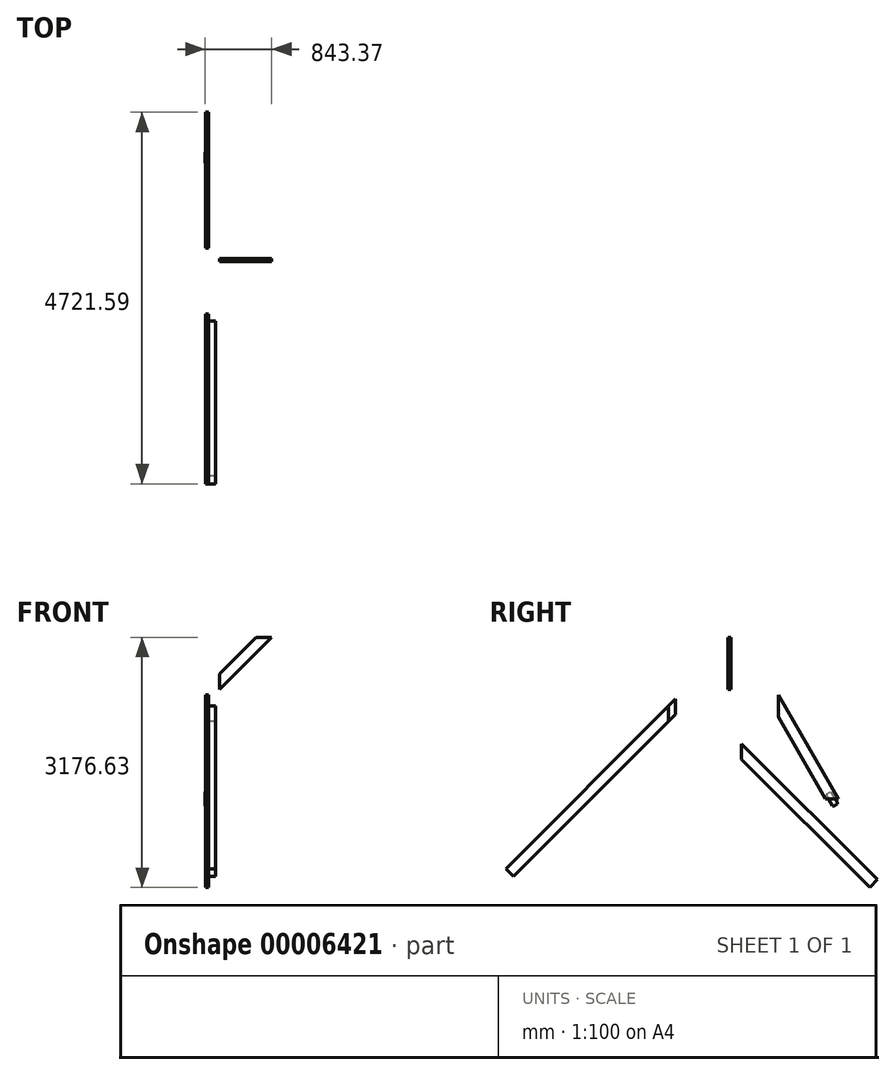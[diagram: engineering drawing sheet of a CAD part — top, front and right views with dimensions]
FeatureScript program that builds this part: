
annotation { "Feature Type Name" : "Feature", "Feature Type Description" : "" }
export const myFeature = defineFeature(function(context is Context, id is Id, definition is map)
    precondition{}
    {
        {
            var Q0;
            Q0=qCreatedBy(makeId("Front.planeOp"),FACE);
            var sketch = newSketch(context, id + "F0", { "sketchPlane" : qUnion([Q0])});
            skLineSegment(sketch, "E0", {"start": v(181.36, 197.57) * mm, "end": v(644.2, 660.4) * mm});
            skLineSegment(sketch, "E1", {"start": v(644.2, 660.4) * mm, "end": v(841.76, 660.4) * mm});
            skLineSegment(sketch, "E2", {"start": v(841.76, 660.4) * mm, "end": v(181.36, 0) * mm});
            skLineSegment(sketch, "E3", {"start": v(181.36, 0) * mm, "end": v(181.36, 197.57) * mm});
            skLineSegment(sketch, "E4", {"start": v(181.36, 0) * mm, "end": v(935.54, 0) * mm, "construction": true});
            skSolve(sketch);
        }
        {
            var Q0;
            Q0=makeQuery(id+"F0.imprint","IMPRINT",FACE,{"disambiguationData":[TD([[makeQuery(id+"F0.imprint","IMPRINT",EDGE,{"derivedFrom":sQuery(id+"F0.wireOp",EDGE,"E0")}),-1.0]])]});
            extrude(context, id + "F1", {"entities" : qUnion([Q0]), "depth" : 38.1 * mm});
        }
        {
            var Q0;
            Q0=qCreatedBy(makeId("Right.planeOp"),FACE);
            var sketch = newSketch(context, id + "F2", { "sketchPlane" : qUnion([Q0])});
            skLineSegment(sketch, "E5", {"start": v(-705.66, -124.36) * mm, "end": v(-705.66, -321.92) * mm});
            skLineSegment(sketch, "E6", {"start": v(-705.66, -321.92) * mm, "end": v(-2762.14, -2378.4) * mm});
            skLineSegment(sketch, "E7", {"start": v(-2762.14, -2378.4) * mm, "end": v(-2860.92, -2279.62) * mm});
            skLineSegment(sketch, "E8", {"start": v(-2860.92, -2279.62) * mm, "end": v(-705.66, -124.36) * mm});
            skSolve(sketch);
        }
        {
            var Q0;
            Q0 = qSketchRegion(id + "F2", true);
            extrude(context, id + "F3", {"entities" : qUnion([Q0]), "depth" : 38.1 * mm});
        }
        {
            var Q0;
            Q0=qCreatedBy(makeId("Right.planeOp"),FACE);
            var sketch = newSketch(context, id + "F4", { "sketchPlane" : qUnion([Q0])});
            skLineSegment(sketch, "E9", {"start": v(136.46, -693.23) * mm, "end": v(136.46, -890.8) * mm});
            skLineSegment(sketch, "E10", {"start": v(136.46, -890.8) * mm, "end": v(1761.89, -2516.23) * mm});
            skLineSegment(sketch, "E11", {"start": v(1761.89, -2516.23) * mm, "end": v(1860.67, -2417.44) * mm});
            skLineSegment(sketch, "E12", {"start": v(1860.67, -2417.44) * mm, "end": v(136.46, -693.23) * mm});
            skSolve(sketch);
        }
        {
            var Q0;
            Q0 = qSketchRegion(id + "F4", true);
            extrude(context, id + "F5", {"entities" : qUnion([Q0]), "depth" : 38.1 * mm});
        }
        {
            var Q0;
            Q0=qCreatedBy(makeId("Right.planeOp"),FACE);
            var sketch = newSketch(context, id + "F6", { "sketchPlane" : qUnion([Q0])});
            skLineSegment(sketch, "E13", {"start": v(601.15, -72.16) * mm, "end": v(601.15, -351.56) * mm});
            skLineSegment(sketch, "E14", {"start": v(601.15, -351.56) * mm, "end": v(1201.84, -1391.98) * mm});
            skLineSegment(sketch, "E15", {"start": v(1201.84, -1391.98) * mm, "end": v(1363.15, -1391.98) * mm});
            skLineSegment(sketch, "E16", {"start": v(1363.15, -1391.98) * mm, "end": v(601.15, -72.16) * mm});
            skSolve(sketch);
        }
        {
            var Q0;
            Q0 = qSketchRegion(id + "F6", true);
            extrude(context, id + "F7", {"entities" : qUnion([Q0]), "depth" : 38.1 * mm});
        }
        {
            var Q0;
            Q0=makeQuery(id+"F7.opExtrude","CAP_FACE",FACE,{"disambiguationData":[OSD([sQuery(id+"F6.wireOp",EDGE,"E13"),sQuery(id+"F6.wireOp",EDGE,"E14"),sQuery(id+"F6.wireOp",EDGE,"E15"),sQuery(id+"F6.wireOp",EDGE,"E16")])],"isStart":true});
            var sketch = newSketch(context, id + "F8", { "sketchPlane" : qUnion([Q0])});
            skLineSegment(sketch, "E17", {"start": v(-1206.16, -1335.97) * mm, "end": v(-1295.06, -1489.95) * mm});
            skLineSegment(sketch, "E18", {"start": v(-1361.05, -1451.85) * mm, "end": v(-1295.06, -1489.95) * mm});
            skLineSegment(sketch, "E19", {"start": v(-1361.05, -1451.85) * mm, "end": v(-1272.15, -1297.87) * mm});
            skLineSegment(sketch, "E20", {"start": v(-1206.16, -1335.97) * mm, "end": v(-1272.15, -1297.87) * mm});
            skLineSegment(sketch, "E21", {"start": v(-1299.65, -1282) * mm, "end": v(-1178.66, -1351.85) * mm, "construction": true});
            skPoint(sketch, "E22", {"position": v(-1239.16, -1316.92) * mm});
            skSolve(sketch);
        }
        {
            var Q0;
            Q0 = qSketchRegion(id + "F8", true);
            extrude(context, id + "F9", {"entities" : qUnion([Q0]), "depth" : 1.61 * mm});
        }
        {
            var Q0;
            Q0=makeQuery(id+"F9.opExtrude","SWEPT_EDGE",EDGE,{"disambiguationData":[OSD([sQuery(id+"F8.wireOp",EDGE,"E19"),sQuery(id+"F8.wireOp",EDGE,"E20")])]});
            var Q1;
            Q1=makeQuery(id+"F9.opExtrude","SWEPT_EDGE",EDGE,{"disambiguationData":[OSD([sQuery(id+"F8.wireOp",EDGE,"E17"),sQuery(id+"F8.wireOp",EDGE,"E20")])]});
            var Q2;
            Q2=makeQuery(id+"F9.opExtrude","SWEPT_EDGE",EDGE,{"disambiguationData":[OSD([sQuery(id+"F8.wireOp",EDGE,"E17"),sQuery(id+"F8.wireOp",EDGE,"E18")])]});
            var Q3;
            Q3=makeQuery(id+"F9.opExtrude","SWEPT_EDGE",EDGE,{"disambiguationData":[OSD([sQuery(id+"F8.wireOp",EDGE,"E18"),sQuery(id+"F8.wireOp",EDGE,"E19")])]});
            chamfer(context, id + "F10", {"entities" : qUnion([Q0, Q1, Q2, Q3]), "width" : 12.7 * mm, "tangentPropagation" : true});
        }
        {
            var Q0;
            Q0=makeQuery(id+"F3.opExtrude","CAP_FACE",FACE,{"disambiguationData":[OSD([sQuery(id+"F2.wireOp",EDGE,"E5"),sQuery(id+"F2.wireOp",EDGE,"E6"),sQuery(id+"F2.wireOp",EDGE,"E7"),sQuery(id+"F2.wireOp",EDGE,"E8")])],"isStart":false});
            var sketch = newSketch(context, id + "F11", { "sketchPlane" : qUnion([Q0])});
            skLineSegment(sketch, "E23", {"start": v(-794.56, -213.26) * mm, "end": v(-794.56, -410.82) * mm});
            skLineSegment(sketch, "E24", {"start": v(-794.56, -410.82) * mm, "end": v(-2762.14, -2378.4) * mm});
            skLineSegment(sketch, "E25", {"start": v(-2762.14, -2378.4) * mm, "end": v(-2860.92, -2279.62) * mm});
            skLineSegment(sketch, "E26", {"start": v(-2860.92, -2279.62) * mm, "end": v(-794.56, -213.26) * mm});
            skSolve(sketch);
        }
        {
            var Q0;
            Q0 = qSketchRegion(id + "F11", true);
            extrude(context, id + "F12", {"entities" : qUnion([Q0]), "depth" : 88.9 * mm});
        }
    });
